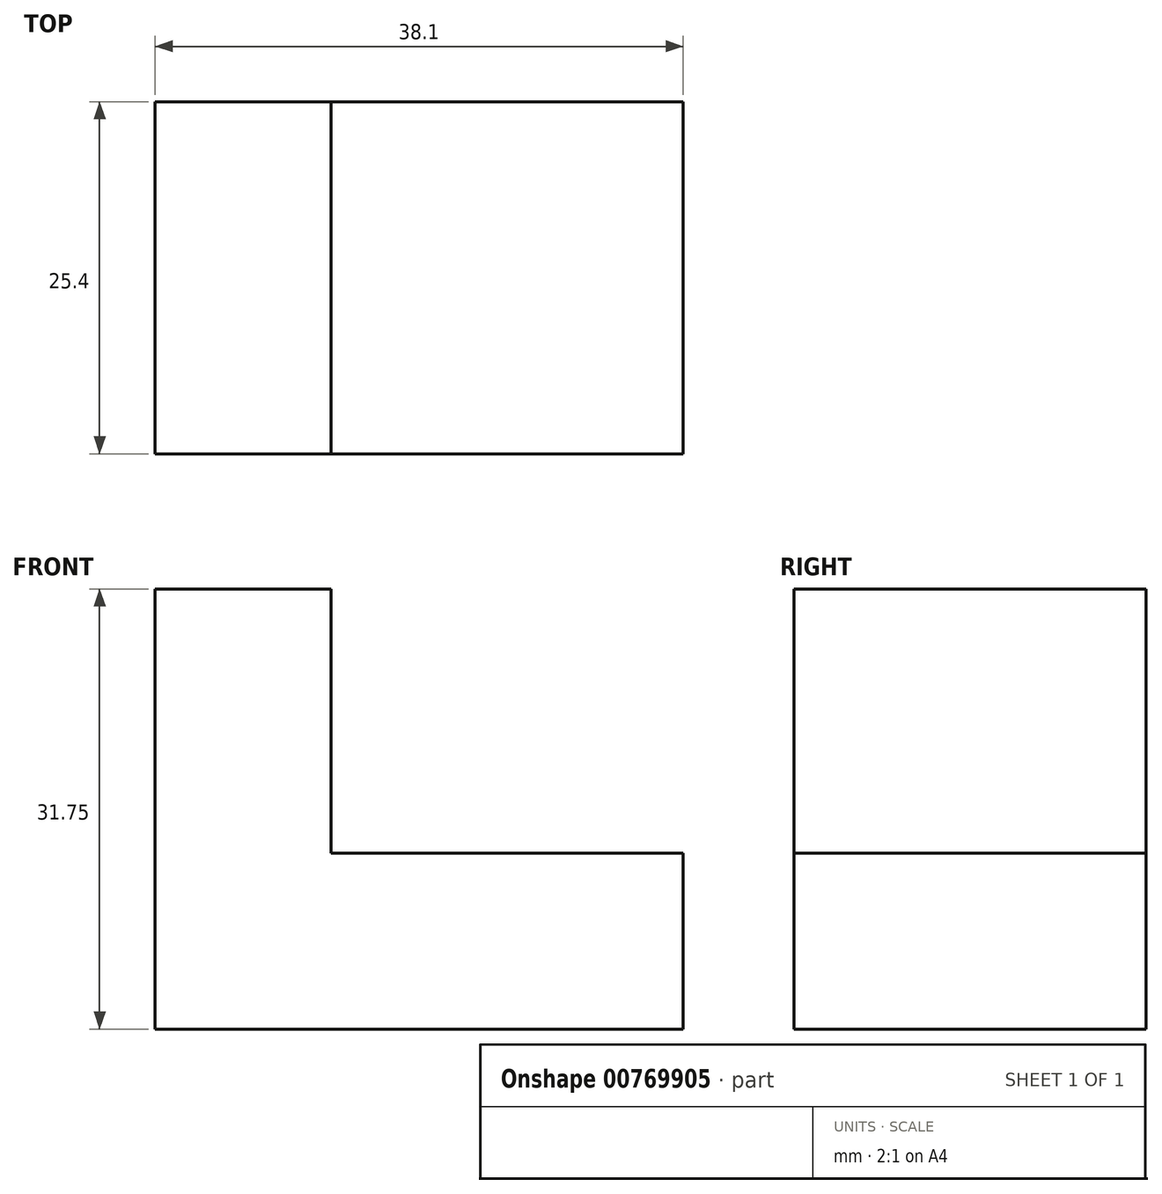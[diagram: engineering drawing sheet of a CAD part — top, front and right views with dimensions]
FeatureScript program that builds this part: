
annotation { "Feature Type Name" : "Feature", "Feature Type Description" : "" }
export const myFeature = defineFeature(function(context is Context, id is Id, definition is map)
    precondition{}
    {
        {
            var Q0;
            Q0=qCreatedBy(makeId("Front.planeOp"),FACE);
            var sketch = newSketch(context, id + "F0", { "sketchPlane" : qUnion([Q0])});
            skLineSegment(sketch, "E0", {"start": v(0, 0) * mm, "end": v(38.1, 0) * mm});
            skLineSegment(sketch, "E1", {"start": v(38.1, 0) * mm, "end": v(38.1, 12.7) * mm});
            skLineSegment(sketch, "E2", {"start": v(12.7, 12.7) * mm, "end": v(38.1, 12.7) * mm});
            skLineSegment(sketch, "E3", {"start": v(12.7, 12.7) * mm, "end": v(12.7, 31.75) * mm});
            skLineSegment(sketch, "E4", {"start": v(12.7, 31.75) * mm, "end": v(0, 31.75) * mm});
            skLineSegment(sketch, "E5", {"start": v(0, 31.75) * mm, "end": v(0, 0) * mm});
            skSolve(sketch);
        }
        {
            var Q0;
            Q0 = qSketchRegion(id + "F0", true);
            extrude(context, id + "F1", {"entities" : qUnion([Q0]), "depth" : 25.4 * mm, "offsetDistance" : 25.4 * mm});
        }
    });
